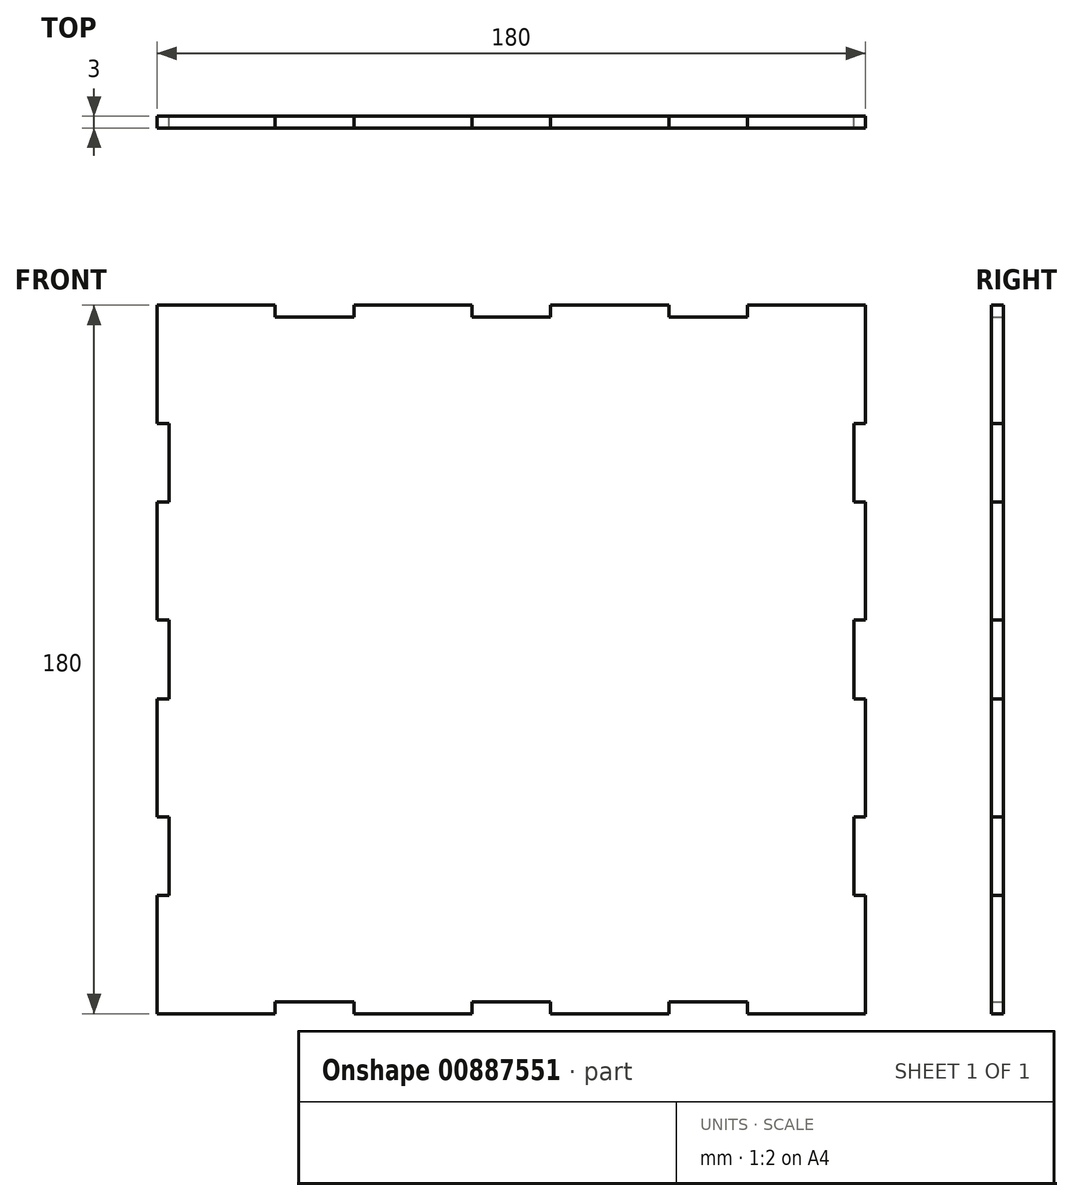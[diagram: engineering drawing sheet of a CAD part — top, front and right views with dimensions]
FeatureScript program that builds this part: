
annotation { "Feature Type Name" : "Feature", "Feature Type Description" : "" }
export const myFeature = defineFeature(function(context is Context, id is Id, definition is map)
    precondition{}
    {
        {
            var Q0;
            Q0=qCreatedBy(makeId("Front.planeOp"),FACE);
            var sketch = newSketch(context, id + "F0", { "sketchPlane" : qUnion([Q0])});
            skLineSegment(sketch, "E0.bottom", {"start": v(90, -90) * mm, "end": v(60, -90) * mm});
            skLineSegment(sketch, "E0.top", {"start": v(90, 90) * mm, "end": v(60, 90) * mm});
            skLineSegment(sketch, "E0.left", {"start": v(90, -90) * mm, "end": v(90, -10) * mm});
            skLineSegment(sketch, "E0.right", {"start": v(-90, -90) * mm, "end": v(-90, -60) * mm});
            skPoint(sketch, "E0.middle", {"position": v(0, 0) * mm});
            skLineSegment(sketch, "E1.top", {"start": v(-40, -87) * mm, "end": v(-60, -87) * mm});
            skLineSegment(sketch, "E1.left", {"start": v(-40, -90) * mm, "end": v(-40, -87) * mm});
            skLineSegment(sketch, "E1.right", {"start": v(-60, -90) * mm, "end": v(-60, -87) * mm});
            skPoint(sketch, "E1.middle", {"position": v(-50, -88.5) * mm});
            skLineSegment(sketch, "E2.top", {"start": v(10, -87) * mm, "end": v(-10, -87) * mm});
            skLineSegment(sketch, "E2.left", {"start": v(10, -90) * mm, "end": v(10, -87) * mm});
            skLineSegment(sketch, "E2.right", {"start": v(-10, -90) * mm, "end": v(-10, -87) * mm});
            skPoint(sketch, "E2.middle", {"position": v(0, -88.5) * mm});
            skLineSegment(sketch, "E3.MirrorCS", {"start": v(40, -87) * mm, "end": v(60, -87) * mm});
            skLineSegment(sketch, "E4.MirrorCS", {"start": v(40, -90) * mm, "end": v(40, -87) * mm});
            skLineSegment(sketch, "E5.MirrorCS", {"start": v(60, -90) * mm, "end": v(60, -87) * mm});
            skLineSegment(sketch, "E6.MirrorCS", {"start": v(-40, 87) * mm, "end": v(-60, 87) * mm});
            skLineSegment(sketch, "E7.MirrorCS", {"start": v(-60, 90) * mm, "end": v(-60, 87) * mm});
            skLineSegment(sketch, "E8.MirrorCS", {"start": v(-40, 90) * mm, "end": v(-40, 87) * mm});
            skLineSegment(sketch, "E9.MirrorCS", {"start": v(-10, 90) * mm, "end": v(-10, 87) * mm});
            skLineSegment(sketch, "E10.MirrorCS", {"start": v(10, 87) * mm, "end": v(-10, 87) * mm});
            skLineSegment(sketch, "E11.MirrorCS", {"start": v(10, 90) * mm, "end": v(10, 87) * mm});
            skLineSegment(sketch, "E12.MirrorCS", {"start": v(40, 87) * mm, "end": v(60, 87) * mm});
            skLineSegment(sketch, "E13.MirrorCS", {"start": v(40, 90) * mm, "end": v(40, 87) * mm});
            skLineSegment(sketch, "E14.MirrorCS", {"start": v(60, 90) * mm, "end": v(60, 87) * mm});
            skLineSegment(sketch, "E15.bottom", {"start": v(90, 40) * mm, "end": v(87, 40) * mm});
            skLineSegment(sketch, "E15.top", {"start": v(90, 60) * mm, "end": v(87, 60) * mm});
            skLineSegment(sketch, "E15.right", {"start": v(87, 40) * mm, "end": v(87, 60) * mm});
            skPoint(sketch, "E15.middle", {"position": v(88.5, 50) * mm});
            skLineSegment(sketch, "E16.bottom", {"start": v(90, -10) * mm, "end": v(87, -10) * mm});
            skLineSegment(sketch, "E16.top", {"start": v(90, 10) * mm, "end": v(87, 10) * mm});
            skLineSegment(sketch, "E16.right", {"start": v(87, -10) * mm, "end": v(87, 10) * mm});
            skPoint(sketch, "E16.middle", {"position": v(88.5, 0) * mm});
            skLineSegment(sketch, "E17.MirrorCS", {"start": v(90, -60) * mm, "end": v(87, -60) * mm});
            skLineSegment(sketch, "E18.MirrorCS", {"start": v(87, -40) * mm, "end": v(87, -60) * mm});
            skLineSegment(sketch, "E19.MirrorCS", {"start": v(90, -40) * mm, "end": v(90, -60) * mm});
            skLineSegment(sketch, "E20.MirrorCS", {"start": v(90, -40) * mm, "end": v(87, -40) * mm});
            skLineSegment(sketch, "E21.MirrorCS", {"start": v(-87, -40) * mm, "end": v(-87, -60) * mm});
            skLineSegment(sketch, "E22.MirrorCS", {"start": v(-90, -60) * mm, "end": v(-87, -60) * mm});
            skLineSegment(sketch, "E23.MirrorCS", {"start": v(-90, -40) * mm, "end": v(-87, -40) * mm});
            skLineSegment(sketch, "E24.MirrorCS", {"start": v(-90, 10) * mm, "end": v(-87, 10) * mm});
            skLineSegment(sketch, "E25.MirrorCS", {"start": v(-87, -10) * mm, "end": v(-87, 10) * mm});
            skLineSegment(sketch, "E26.MirrorCS", {"start": v(-90, -10) * mm, "end": v(-87, -10) * mm});
            skLineSegment(sketch, "E27.MirrorCS", {"start": v(-87, 40) * mm, "end": v(-87, 60) * mm});
            skLineSegment(sketch, "E28.MirrorCS", {"start": v(-90, 40) * mm, "end": v(-87, 40) * mm});
            skLineSegment(sketch, "E29.MirrorCS", {"start": v(-90, 60) * mm, "end": v(-87, 60) * mm});
            skLineSegment(sketch, "E30.trimOffspring", {"start": v(-60, -90) * mm, "end": v(-90, -90) * mm});
            skLineSegment(sketch, "E31.trimOffspring", {"start": v(-10, -90) * mm, "end": v(-40, -90) * mm});
            skPoint(sketch, "E32.MirrorCS.end.orphan", {"position": v(60, -90) * mm});
            skPoint(sketch, "E32.MirrorCS.start.orphan", {"position": v(40, -90) * mm});
            skLineSegment(sketch, "E33.trimOffspring", {"start": v(40, -90) * mm, "end": v(10, -90) * mm});
            skLineSegment(sketch, "E34.trimOffspring", {"start": v(90, 60) * mm, "end": v(90, 90) * mm});
            skLineSegment(sketch, "E35.trimOffspring", {"start": v(90, 10) * mm, "end": v(90, 40) * mm});
            skPoint(sketch, "E36.MirrorCS.end.orphan", {"position": v(-10, 90) * mm});
            skPoint(sketch, "E36.MirrorCS.start.orphan", {"position": v(10, 90) * mm});
            skLineSegment(sketch, "E37.trimOffspring", {"start": v(-10, 90) * mm, "end": v(-40, 90) * mm});
            skPoint(sketch, "E38.MirrorCS.end.orphan", {"position": v(-60, 90) * mm});
            skPoint(sketch, "E38.MirrorCS.start.orphan", {"position": v(-40, 90) * mm});
            skLineSegment(sketch, "E39.trimOffspring", {"start": v(-60, 90) * mm, "end": v(-90, 90) * mm});
            skPoint(sketch, "E40.MirrorCS.end.orphan", {"position": v(60, 90) * mm});
            skPoint(sketch, "E40.MirrorCS.start.orphan", {"position": v(40, 90) * mm});
            skLineSegment(sketch, "E41.trimOffspring", {"start": v(40, 90) * mm, "end": v(10, 90) * mm});
            skPoint(sketch, "E42.MirrorCS.end.orphan", {"position": v(-90, -60) * mm});
            skPoint(sketch, "E42.MirrorCS.start.orphan", {"position": v(-90, -40) * mm});
            skLineSegment(sketch, "E43.trimOffspring", {"start": v(-90, -40) * mm, "end": v(-90, -10) * mm});
            skLineSegment(sketch, "E44.trimOffspring", {"start": v(-90, 10) * mm, "end": v(-90, 40) * mm});
            skLineSegment(sketch, "E45.trimOffspring", {"start": v(-90, 60) * mm, "end": v(-90, 90) * mm});
            skPoint(sketch, "E46.MirrorCS.end.orphan", {"position": v(-90, 60) * mm});
            skPoint(sketch, "E46.MirrorCS.start.orphan", {"position": v(-90, 40) * mm});
            skSolve(sketch);
        }
        {
            var Q0;
            Q0=makeQuery(id+"F0.imprint","IMPRINT",FACE,{"disambiguationData":[TD([[makeQuery(id+"F0.imprint","IMPRINT",EDGE,{"derivedFrom":sQuery(id+"F0.wireOp",EDGE,"E0.bottom")}),-1.0]])]});
            extrude(context, id + "F1", {"entities" : qUnion([Q0]), "depth" : 3 * mm, "offsetDistance" : 25 * mm});
        }
    });
